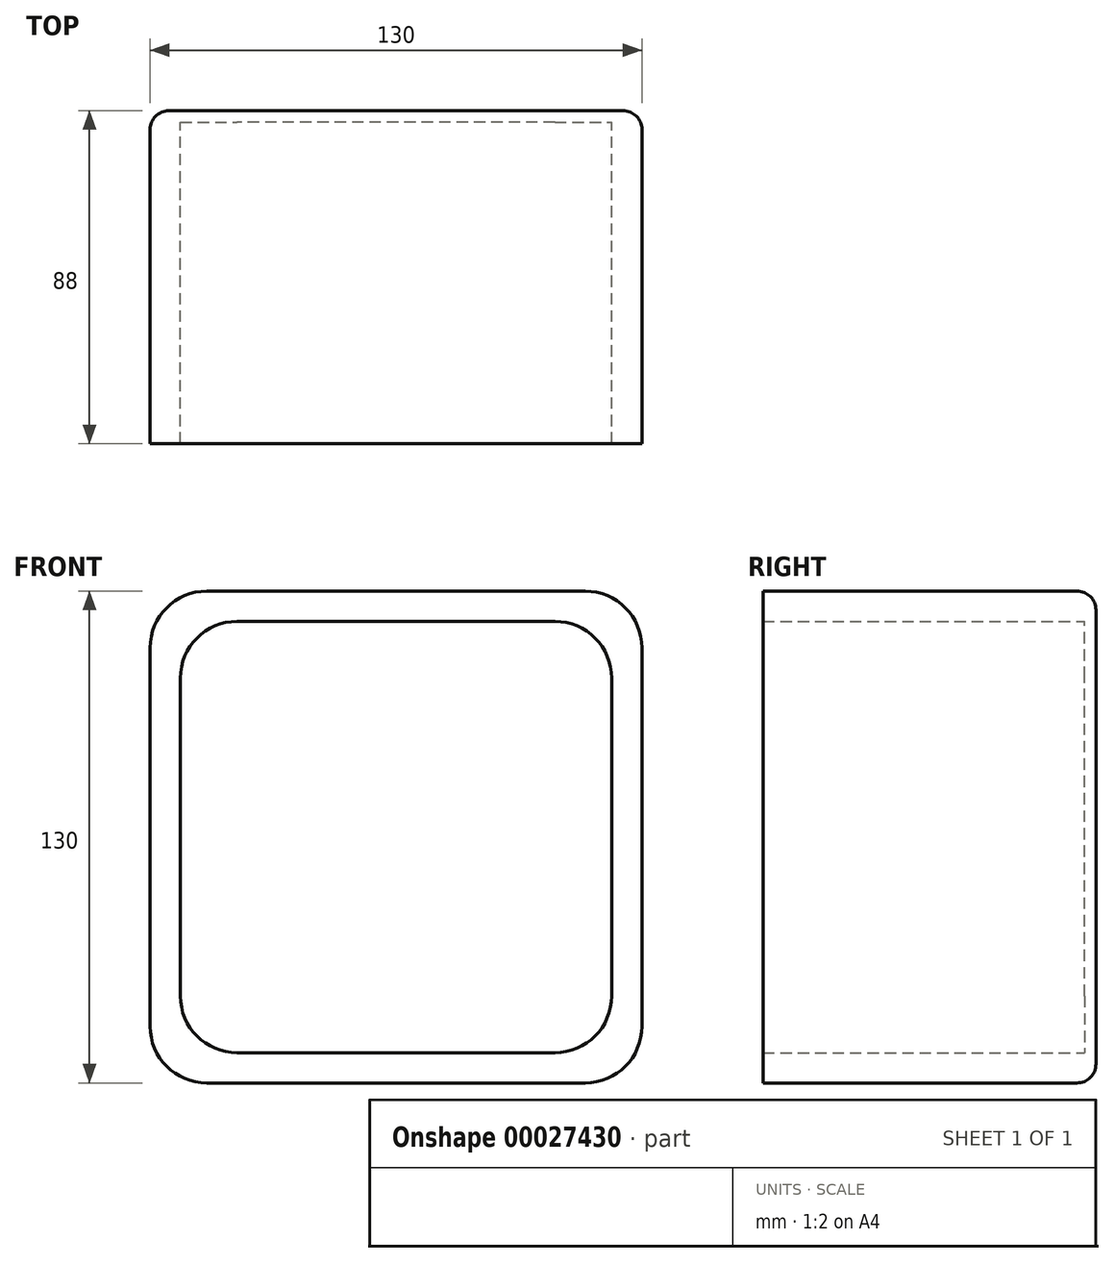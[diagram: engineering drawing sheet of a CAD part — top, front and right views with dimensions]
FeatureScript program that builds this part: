
annotation { "Feature Type Name" : "Feature", "Feature Type Description" : "" }
export const myFeature = defineFeature(function(context is Context, id is Id, definition is map)
    precondition{}
    {
        {
            var Q0;
            Q0=qCreatedBy(makeId("Front.planeOp"),FACE);
            var sketch = newSketch(context, id + "F0", { "sketchPlane" : qUnion([Q0])});
            skLineSegment(sketch, "E0.rect.bottom", {"start": v(65, -65) * mm, "end": v(-65, -65) * mm});
            skLineSegment(sketch, "E0.rect.top", {"start": v(65, 65) * mm, "end": v(-65, 65) * mm});
            skLineSegment(sketch, "E0.rect.left", {"start": v(65, -65) * mm, "end": v(65, 65) * mm});
            skLineSegment(sketch, "E0.rect.right", {"start": v(-65, -65) * mm, "end": v(-65, 65) * mm});
            skPoint(sketch, "E0.rect.middle", {"position": v(0, 0) * mm});
            skLineSegment(sketch, "E1.rect.bottom", {"start": v(57, -57) * mm, "end": v(-57, -57) * mm});
            skLineSegment(sketch, "E1.rect.top", {"start": v(57, 57) * mm, "end": v(-57, 57) * mm});
            skLineSegment(sketch, "E1.rect.left", {"start": v(57, -57) * mm, "end": v(57, 57) * mm});
            skLineSegment(sketch, "E1.rect.right", {"start": v(-57, -57) * mm, "end": v(-57, 57) * mm});
            skSolve(sketch);
        }
        {
            var Q0;
            Q0=makeQuery(id+"F0.imprint","IMPRINT",FACE,{"disambiguationData":[TD([[makeQuery(id+"F0.imprint","IMPRINT",EDGE,{"derivedFrom":sQuery(id+"F0.wireOp",EDGE,"E0.rect.bottom")}),-1.0]])]});
            extrude(context, id + "F1", {"entities" : qUnion([Q0]), "depth" : 85 * mm});
        }
        {
            var Q0;
            Q0=makeQuery(id+"F1.opExtrude","SWEPT_EDGE",EDGE,{"disambiguationData":[OSD([sQuery(id+"F0.wireOp",EDGE,"E0.rect.top"),sQuery(id+"F0.wireOp",EDGE,"E0.rect.right")])]});
            var Q1;
            Q1=makeQuery(id+"F1.opExtrude","SWEPT_EDGE",EDGE,{"disambiguationData":[OSD([sQuery(id+"F0.wireOp",EDGE,"E1.rect.top"),sQuery(id+"F0.wireOp",EDGE,"E1.rect.right")])]});
            var Q2;
            Q2=makeQuery(id+"F1.opExtrude","SWEPT_EDGE",EDGE,{"disambiguationData":[OSD([sQuery(id+"F0.wireOp",EDGE,"E0.rect.top"),sQuery(id+"F0.wireOp",EDGE,"E0.rect.left")])]});
            var Q3;
            Q3=makeQuery(id+"F1.opExtrude","SWEPT_EDGE",EDGE,{"disambiguationData":[OSD([sQuery(id+"F0.wireOp",EDGE,"E1.rect.top"),sQuery(id+"F0.wireOp",EDGE,"E1.rect.left")])]});
            var Q4;
            Q4=makeQuery(id+"F1.opExtrude","SWEPT_EDGE",EDGE,{"disambiguationData":[OSD([sQuery(id+"F0.wireOp",EDGE,"E0.rect.bottom"),sQuery(id+"F0.wireOp",EDGE,"E0.rect.left")])]});
            var Q5;
            Q5=makeQuery(id+"F1.opExtrude","SWEPT_EDGE",EDGE,{"disambiguationData":[OSD([sQuery(id+"F0.wireOp",EDGE,"E1.rect.bottom"),sQuery(id+"F0.wireOp",EDGE,"E1.rect.left")])]});
            var Q6;
            Q6=makeQuery(id+"F1.opExtrude","SWEPT_EDGE",EDGE,{"disambiguationData":[OSD([sQuery(id+"F0.wireOp",EDGE,"E1.rect.bottom"),sQuery(id+"F0.wireOp",EDGE,"E1.rect.right")])]});
            var Q7;
            Q7=makeQuery(id+"F1.opExtrude","SWEPT_EDGE",EDGE,{"disambiguationData":[OSD([sQuery(id+"F0.wireOp",EDGE,"E0.rect.bottom"),sQuery(id+"F0.wireOp",EDGE,"E0.rect.right")])]});
            fillet(context, id + "F2", {"entities" : qUnion([Q0, Q1, Q2, Q3, Q4, Q5, Q6, Q7]), "radius" : 15 * mm, "tangentPropagation" : true, "allowEdgeOverflow" : false});
        }
        {
            var Q0;
            Q0=makeQuery(id+"F1.opExtrude","CAP_FACE",FACE,{"disambiguationData":[OSD([sQuery(id+"F0.wireOp",EDGE,"E0.rect.bottom"),sQuery(id+"F0.wireOp",EDGE,"E0.rect.top"),sQuery(id+"F0.wireOp",EDGE,"E0.rect.left"),sQuery(id+"F0.wireOp",EDGE,"E0.rect.right"),sQuery(id+"F0.wireOp",EDGE,"E1.rect.bottom"),sQuery(id+"F0.wireOp",EDGE,"E1.rect.top"),sQuery(id+"F0.wireOp",EDGE,"E1.rect.left"),sQuery(id+"F0.wireOp",EDGE,"E1.rect.right")])],"isStart":true});
            var sketch = newSketch(context, id + "F3", { "sketchPlane" : qUnion([Q0])});
            skLineSegment(sketch, "E2.rect.bottom", {"start": v(50, -65) * mm, "end": v(-50, -65) * mm});
            skLineSegment(sketch, "E2.rect.top", {"start": v(50, 65) * mm, "end": v(-50, 65) * mm});
            skLineSegment(sketch, "E2.rect.left", {"start": v(65, -50) * mm, "end": v(65, 50) * mm});
            skLineSegment(sketch, "E2.rect.right", {"start": v(-65, -50) * mm, "end": v(-65, 50) * mm});
            skPoint(sketch, "E2.rect.middle", {"position": v(0, 0) * mm});
            skPoint(sketch, "E3.visualSharp", {"position": v(-65, 65) * mm});
            skArc(sketch, "E3.filletArc", {"start": v(-50, 65) * mm, "mid": v(-60.6, 60.6) * mm, "end": v(-65, 50) * mm});
            skPoint(sketch, "E4.visualSharp", {"position": v(65, 65) * mm});
            skArc(sketch, "E4.filletArc", {"start": v(65, 50) * mm, "mid": v(60.6, 60.6) * mm, "end": v(50, 65) * mm});
            skPoint(sketch, "E5.visualSharp", {"position": v(65, -65) * mm});
            skArc(sketch, "E5.filletArc", {"start": v(50, -65) * mm, "mid": v(60.6, -60.6) * mm, "end": v(65, -50) * mm});
            skPoint(sketch, "E6.visualSharp", {"position": v(-65, -65) * mm});
            skArc(sketch, "E6.filletArc", {"start": v(-65, -50) * mm, "mid": v(-60.6, -60.6) * mm, "end": v(-50, -65) * mm});
            skSolve(sketch);
        }
        {
            var Q0;
            Q0 = qSketchRegion(id + "F3", true);
            extrude(context, id + "F4", {"entities" : qUnion([Q0]), "operationType" : NewBodyOperationType.ADD, "depth" : 3 * mm});
        }
        {
            var Q0;
            Q0=makeQuery(id+"F4.opExtrude","CAP_EDGE",EDGE,{"disambiguationData":[OSD([sQuery(id+"F3.wireOp",EDGE,"E6.filletArc")])],"isStart":false});
            fillet(context, id + "F5", {"entities" : qUnion([Q0]), "radius" : 5 * mm, "tangentPropagation" : true, "allowEdgeOverflow" : false});
        }
    });
